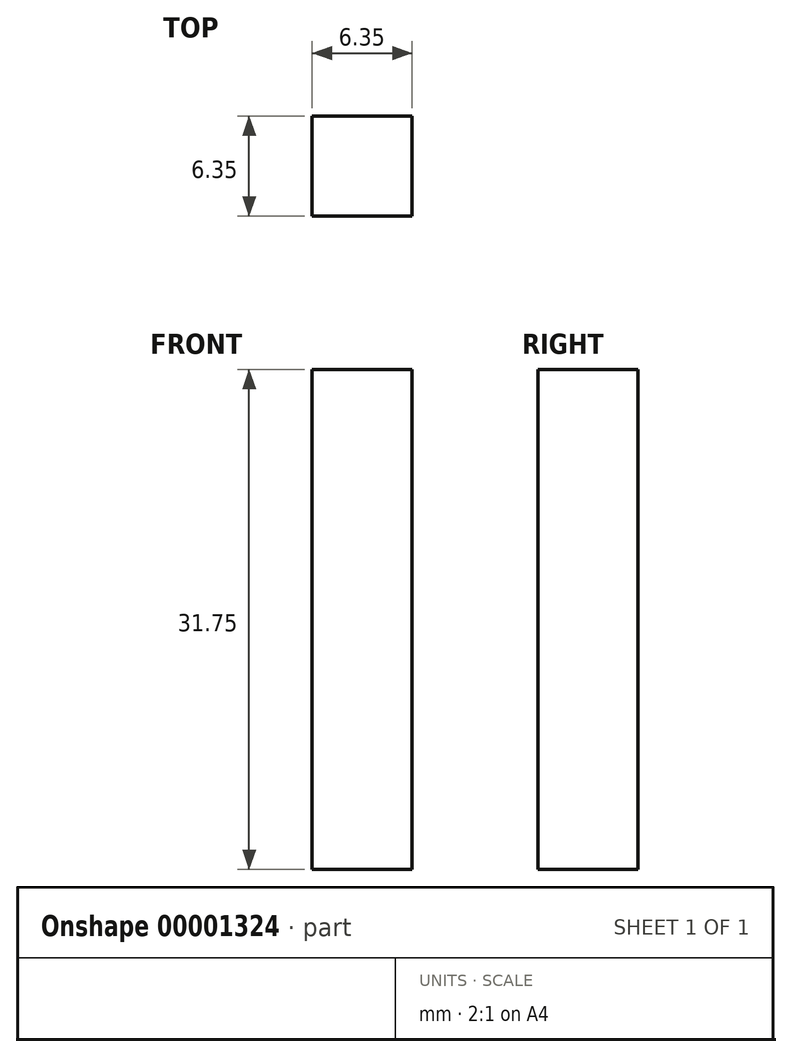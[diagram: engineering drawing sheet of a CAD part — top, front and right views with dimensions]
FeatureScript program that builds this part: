
annotation { "Feature Type Name" : "Feature", "Feature Type Description" : "" }
export const myFeature = defineFeature(function(context is Context, id is Id, definition is map)
    precondition{}
    {
        {
            var Q0;
            Q0=qCreatedBy(makeId("Front.planeOp"),FACE);
            var sketch = newSketch(context, id + "F0", { "sketchPlane" : qUnion([Q0])});
            skLineSegment(sketch, "E0.bottom", {"start": v(0, 0) * mm, "end": v(-6.35, 0) * mm});
            skLineSegment(sketch, "E0.top", {"start": v(0, -31.75) * mm, "end": v(-6.35, -31.75) * mm});
            skLineSegment(sketch, "E0.left", {"start": v(0, 0) * mm, "end": v(0, -31.75) * mm});
            skLineSegment(sketch, "E0.right", {"start": v(-6.35, 0) * mm, "end": v(-6.35, -31.75) * mm});
            skSolve(sketch);
        }
        {
            var Q0;
            Q0=makeQuery(id+"F0.imprint","IMPRINT",FACE,{"disambiguationData":[TD([[makeQuery(id+"F0.imprint","IMPRINT",EDGE,{"derivedFrom":sQuery(id+"F0.wireOp",EDGE,"E0.bottom")}),1.0]])]});
            extrude(context, id + "F1", {"entities" : qUnion([Q0]), "oppositeDirection" : true, "depth" : 6.35 * mm});
        }
    });
